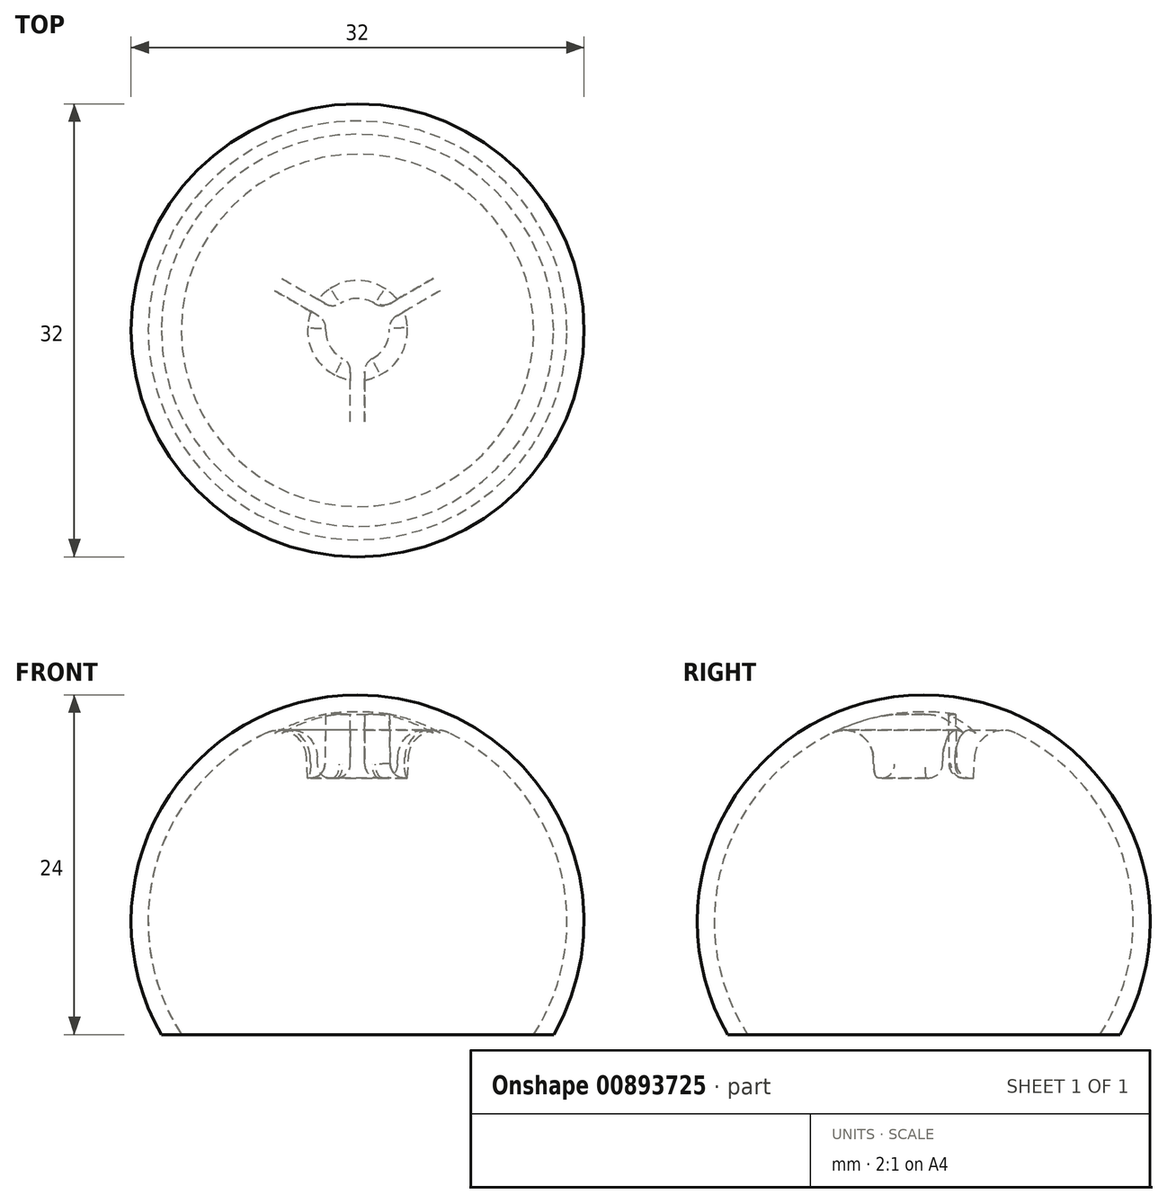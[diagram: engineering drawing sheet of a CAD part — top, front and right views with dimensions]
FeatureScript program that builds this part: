
annotation { "Feature Type Name" : "Feature", "Feature Type Description" : "" }
export const myFeature = defineFeature(function(context is Context, id is Id, definition is map)
    precondition{}
    {
        {
            var Q0;
            Q0=qCreatedBy(makeId("Front.planeOp"),FACE);
            var sketch = newSketch(context, id + "F0", { "sketchPlane" : qUnion([Q0])});
            skArc(sketch, "E0", {"start": v(0, 24) * mm, "mid": v(-13.86, 16) * mm, "end": v(-13.86, 0) * mm});
            skPoint(sketch, "E1", {"position": v(0, 24) * mm});
            skArc(sketch, "E2.0", {"start": v(0, 22.8) * mm, "mid": v(-12.99, 15.1) * mm, "end": v(-12.45, 0) * mm});
            skLineSegment(sketch, "E3", {"start": v(-13.86, 0) * mm, "end": v(-12.45, 0) * mm});
            skPoint(sketch, "E4.orphan", {"position": v(12.45, 0) * mm});
            skPoint(sketch, "E5.orphan", {"position": v(13.86, 0) * mm});
            skLineSegment(sketch, "E6", {"start": v(-3.75, 22.32) * mm, "end": v(-3.53, 18.13) * mm});
            skLineSegment(sketch, "E7", {"start": v(-3.53, 18.13) * mm, "end": v(-2.33, 18.13) * mm});
            skLineSegment(sketch, "E8", {"start": v(-2.33, 18.13) * mm, "end": v(-2.25, 22.63) * mm});
            skLineSegment(sketch, "E9", {"start": v(0, 22.8) * mm, "end": v(0, 24) * mm});
            skSolve(sketch);
        }
        {
            var Q0;
            Q0 = qSketchRegion(id + "F0", true);
            var Q1;
            Q1=sQuery(id+"F0.wireOp",EDGE,"E9");
            revolve(context, id + "F1", {"surfaceOperationType" : NewSurfaceOperationType.NEW, "entities" : qUnion([Q0]), "axis" : qUnion([Q1]), "revolveType" : RevolveType.FULL});
        }
        {
            var Q0;
            Q0=qCreatedBy(makeId("Top.planeOp"),FACE);
            var sketch = newSketch(context, id + "F2", { "sketchPlane" : qUnion([Q0])});
            skLineSegment(sketch, "E10.bottom", {"start": v(0.5, -3.75) * mm, "end": v(-0.5, -3.75) * mm});
            skLineSegment(sketch, "E10.top", {"start": v(0.5, -2.2) * mm, "end": v(-0.5, -2.2) * mm});
            skLineSegment(sketch, "E10.left", {"start": v(0.5, -3.75) * mm, "end": v(0.5, -2.2) * mm});
            skLineSegment(sketch, "E10.right", {"start": v(-0.5, -3.75) * mm, "end": v(-0.5, -2.2) * mm});
            skPoint(sketch, "E10.middle", {"position": v(0, -2.97) * mm});
            skLineSegment(sketch, "E11.1.0", {"start": v(3, 2.3) * mm, "end": v(1.65, 1.53) * mm});
            skLineSegment(sketch, "E11.1.1", {"start": v(3, 2.3) * mm, "end": v(3.5, 1.44) * mm});
            skLineSegment(sketch, "E11.1.2", {"start": v(3.5, 1.44) * mm, "end": v(2.15, 0.66) * mm});
            skLineSegment(sketch, "E11.1.3", {"start": v(1.65, 1.53) * mm, "end": v(2.15, 0.66) * mm});
            skLineSegment(sketch, "E11.2.0", {"start": v(-3.5, 1.44) * mm, "end": v(-2.15, 0.66) * mm});
            skLineSegment(sketch, "E11.2.1", {"start": v(-3.5, 1.44) * mm, "end": v(-3, 2.3) * mm});
            skLineSegment(sketch, "E11.2.2", {"start": v(-3, 2.3) * mm, "end": v(-1.65, 1.53) * mm});
            skLineSegment(sketch, "E11.2.3", {"start": v(-2.15, 0.66) * mm, "end": v(-1.65, 1.53) * mm});
            skPoint(sketch, "E11.center", {"position": v(0, 0) * mm});
            skSolve(sketch);
        }
        {
            var Q0;
            Q0 = qSketchRegion(id + "F2", true);
            var Q1;
            {var subQ0=sQuery(id+"F0.wireOp",EDGE,"E2.0");Q1=makeQuery(id+"F1.opRevolve","SWEPT_FACE",FACE,{"disambiguationData":[OSD([subQ0]),TDD([makeQuery(id+"F0.imprint","IMPRINT",EDGE,{"disambiguationData":[TD([[makeQuery(id+"F0.imprint","INTERSECT",VERTEX,{"derivedFrom":[subQ0,sQuery(id+"F0.wireOp",EDGE,"E3")]}),1.0]])],"derivedFrom":subQ0})])]});}
            extrude(context, id + "F3", {"entities" : qUnion([Q0]), "operationType" : NewBodyOperationType.REMOVE, "endBound" : BoundingType.UP_TO_SURFACE, "depth" : 25 * mm, "endBoundEntityFace" : qUnion([Q1]), "offsetDistance" : 25 * mm});
        }
        {
            var Q0;
            {var subQ0=sQuery(id+"F0.wireOp",EDGE,"E7");var subQ1=sQuery(id+"F0.wireOp",EDGE,"E8");Q0=makeQuery(id+"F3.boolean.opBoolean","SPLIT",EDGE,{"disambiguationData":[TD([makeQuery(id+"F3.opExtrude","SWEPT_FACE",FACE,{"disambiguationData":[OSD([sQuery(id+"F2.wireOp",EDGE,"E10.left")])]})])],"derivedFrom":makeQuery(id+"F1.opRevolve","SWEPT_EDGE",EDGE,{"disambiguationData":[OSD([subQ0,subQ1])]})});}
            var Q1;
            {var subQ0=sQuery(id+"F0.wireOp",EDGE,"E7");var subQ1=sQuery(id+"F0.wireOp",EDGE,"E8");Q1=makeQuery(id+"F3.boolean.opBoolean","SPLIT",EDGE,{"disambiguationData":[TD([makeQuery(id+"F3.opExtrude","SWEPT_FACE",FACE,{"disambiguationData":[OSD([sQuery(id+"F2.wireOp",EDGE,"E10.right")])]})])],"derivedFrom":makeQuery(id+"F1.opRevolve","SWEPT_EDGE",EDGE,{"disambiguationData":[OSD([subQ0,subQ1])]})});}
            var Q2;
            {var subQ0=sQuery(id+"F0.wireOp",EDGE,"E7");var subQ1=sQuery(id+"F0.wireOp",EDGE,"E8");Q2=makeQuery(id+"F3.boolean.opBoolean","SPLIT",EDGE,{"disambiguationData":[TD([makeQuery(id+"F3.opExtrude","SWEPT_FACE",FACE,{"disambiguationData":[OSD([sQuery(id+"F2.wireOp",EDGE,"E11.1.0")])]})])],"derivedFrom":makeQuery(id+"F1.opRevolve","SWEPT_EDGE",EDGE,{"disambiguationData":[OSD([subQ0,subQ1])]})});}
            fillet(context, id + "F4", {"entities" : qUnion([Q0, Q1, Q2]), "radius" : 1 * mm, "tangentPropagation" : true, "allowEdgeOverflow" : false});
        }
        {
            var Q0;
            Q0=makeQuery(id+"F3.boolean.opBoolean","INTERSECT",EDGE,{"derivedFrom":[makeQuery(id+"F1.opRevolve","SWEPT_FACE",FACE,{"disambiguationData":[OSD([sQuery(id+"F0.wireOp",EDGE,"E8")])]}),makeQuery(id+"F3.opExtrude","SWEPT_FACE",FACE,{"disambiguationData":[OSD([sQuery(id+"F2.wireOp",EDGE,"E11.2.0")])]})]});
            var Q1;
            Q1=makeQuery(id+"F3.boolean.opBoolean","INTERSECT",EDGE,{"derivedFrom":[makeQuery(id+"F1.opRevolve","SWEPT_FACE",FACE,{"disambiguationData":[OSD([sQuery(id+"F0.wireOp",EDGE,"E8")])]}),makeQuery(id+"F3.opExtrude","SWEPT_FACE",FACE,{"disambiguationData":[OSD([sQuery(id+"F2.wireOp",EDGE,"E11.2.2")])]})]});
            var Q2;
            Q2=makeQuery(id+"F3.boolean.opBoolean","INTERSECT",EDGE,{"derivedFrom":[makeQuery(id+"F1.opRevolve","SWEPT_FACE",FACE,{"disambiguationData":[OSD([sQuery(id+"F0.wireOp",EDGE,"E8")])]}),makeQuery(id+"F3.opExtrude","SWEPT_FACE",FACE,{"disambiguationData":[OSD([sQuery(id+"F2.wireOp",EDGE,"E11.1.2")])]})]});
            var Q3;
            Q3=makeQuery(id+"F3.boolean.opBoolean","INTERSECT",EDGE,{"derivedFrom":[makeQuery(id+"F1.opRevolve","SWEPT_FACE",FACE,{"disambiguationData":[OSD([sQuery(id+"F0.wireOp",EDGE,"E8")])]}),makeQuery(id+"F3.opExtrude","SWEPT_FACE",FACE,{"disambiguationData":[OSD([sQuery(id+"F2.wireOp",EDGE,"E11.1.0")])]})]});
            var Q4;
            Q4=makeQuery(id+"F3.boolean.opBoolean","INTERSECT",EDGE,{"derivedFrom":[makeQuery(id+"F1.opRevolve","SWEPT_FACE",FACE,{"disambiguationData":[OSD([sQuery(id+"F0.wireOp",EDGE,"E8")])]}),makeQuery(id+"F3.opExtrude","SWEPT_FACE",FACE,{"disambiguationData":[OSD([sQuery(id+"F2.wireOp",EDGE,"E10.left")])]})]});
            var Q5;
            Q5=makeQuery(id+"F3.boolean.opBoolean","INTERSECT",EDGE,{"derivedFrom":[makeQuery(id+"F1.opRevolve","SWEPT_FACE",FACE,{"disambiguationData":[OSD([sQuery(id+"F0.wireOp",EDGE,"E8")])]}),makeQuery(id+"F3.opExtrude","SWEPT_FACE",FACE,{"disambiguationData":[OSD([sQuery(id+"F2.wireOp",EDGE,"E10.right")])]})]});
            fillet(context, id + "F5", {"entities" : qUnion([Q0, Q1, Q2, Q3, Q4, Q5]), "radius" : 1 * mm, "tangentPropagation" : true, "allowEdgeOverflow" : false});
        }
        {
            var Q0;
            {var subQ0=sQuery(id+"F2.wireOp",EDGE,"E10.right");var subQ1=sQuery(id+"F0.wireOp",EDGE,"E6");var subQ3=sQuery(id+"F0.wireOp",EDGE,"E2.0");Q0=makeQuery(id+"F3.boolean.opBoolean","SPLIT",EDGE,{"disambiguationData":[TD([makeQuery(id+"F3.opExtrude","SWEPT_FACE",FACE,{"disambiguationData":[OSD([subQ0])]})])],"derivedFrom":makeQuery(id+"F1.opRevolve","SWEPT_EDGE",EDGE,{"disambiguationData":[OSD([subQ3,subQ1])]})});}
            var Q1;
            {var subQ0=sQuery(id+"F2.wireOp",EDGE,"E10.left");var subQ1=sQuery(id+"F0.wireOp",EDGE,"E6");var subQ2=sQuery(id+"F0.wireOp",EDGE,"E2.0");Q1=makeQuery(id+"F3.boolean.opBoolean","SPLIT",EDGE,{"disambiguationData":[TD([makeQuery(id+"F3.opExtrude","SWEPT_FACE",FACE,{"disambiguationData":[OSD([subQ0])]})])],"derivedFrom":makeQuery(id+"F1.opRevolve","SWEPT_EDGE",EDGE,{"disambiguationData":[OSD([subQ2,subQ1])]})});}
            var Q2;
            {var subQ0=sQuery(id+"F0.wireOp",EDGE,"E6");var subQ2=sQuery(id+"F0.wireOp",EDGE,"E2.0");var subQ3=sQuery(id+"F2.wireOp",EDGE,"E11.1.0");Q2=makeQuery(id+"F3.boolean.opBoolean","SPLIT",EDGE,{"disambiguationData":[TD([makeQuery(id+"F3.opExtrude","SWEPT_FACE",FACE,{"disambiguationData":[OSD([subQ3])]})])],"derivedFrom":makeQuery(id+"F1.opRevolve","SWEPT_EDGE",EDGE,{"disambiguationData":[OSD([subQ2,subQ0])]})});}
            fillet(context, id + "F6", {"entities" : qUnion([Q0, Q1, Q2]), "radius" : 2 * mm, "tangentPropagation" : true, "allowEdgeOverflow" : false});
        }
    });
